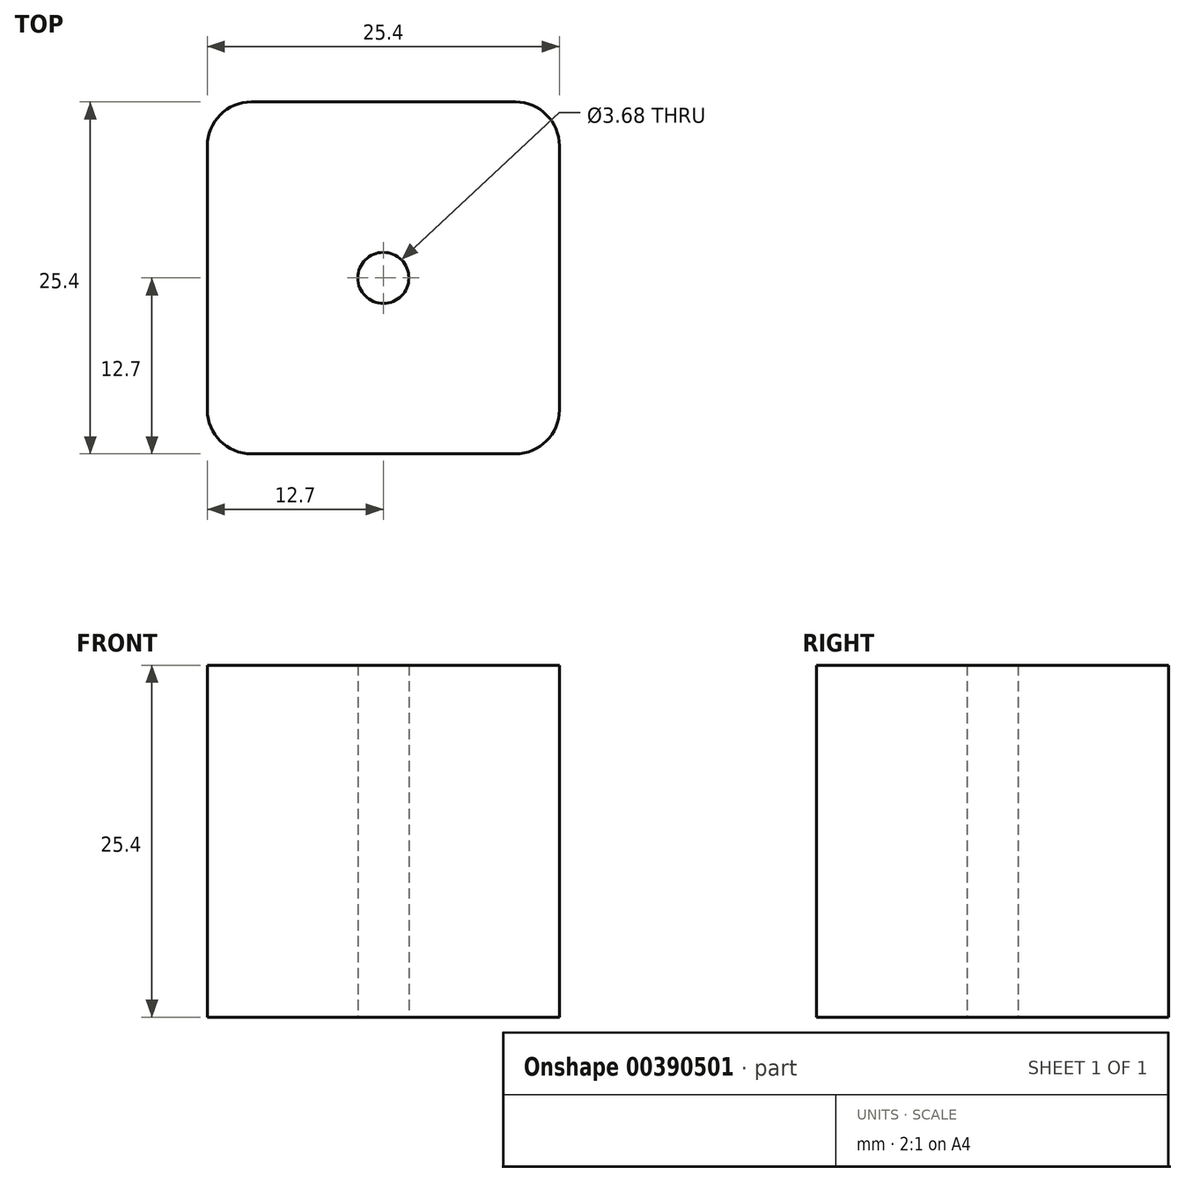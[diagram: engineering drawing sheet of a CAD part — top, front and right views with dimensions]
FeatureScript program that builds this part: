
annotation { "Feature Type Name" : "Feature", "Feature Type Description" : "" }
export const myFeature = defineFeature(function(context is Context, id is Id, definition is map)
    precondition{}
    {
        {
            var Q0;
            Q0=qCreatedBy(makeId("Top.planeOp"),FACE);
            var sketch = newSketch(context, id + "F0", { "sketchPlane" : qUnion([Q0])});
            skLineSegment(sketch, "E0.bottom", {"start": v(-9.53, 12.7) * mm, "end": v(9.53, 12.7) * mm});
            skLineSegment(sketch, "E0.top", {"start": v(-9.52, -12.7) * mm, "end": v(9.52, -12.7) * mm});
            skLineSegment(sketch, "E0.left", {"start": v(-12.7, 9.53) * mm, "end": v(-12.7, -9.52) * mm});
            skLineSegment(sketch, "E0.right", {"start": v(12.7, 9.53) * mm, "end": v(12.7, -9.53) * mm});
            skPoint(sketch, "E0.middle", {"position": v(0, 0) * mm});
            skPoint(sketch, "E1.visualSharp", {"position": v(-12.7, 12.7) * mm});
            skArc(sketch, "E1.filletArc", {"start": v(-9.53, 12.7) * mm, "mid": v(-11.77, 11.77) * mm, "end": v(-12.7, 9.53) * mm});
            skPoint(sketch, "E2.visualSharp", {"position": v(12.7, 12.7) * mm});
            skArc(sketch, "E2.filletArc", {"start": v(12.7, 9.53) * mm, "mid": v(11.77, 11.77) * mm, "end": v(9.53, 12.7) * mm});
            skPoint(sketch, "E3.visualSharp", {"position": v(-12.7, -12.7) * mm});
            skArc(sketch, "E3.filletArc", {"start": v(-12.7, -9.52) * mm, "mid": v(-11.77, -11.77) * mm, "end": v(-9.52, -12.7) * mm});
            skPoint(sketch, "E4.visualSharp", {"position": v(12.7, -12.7) * mm});
            skArc(sketch, "E4.filletArc", {"start": v(9.52, -12.7) * mm, "mid": v(11.77, -11.77) * mm, "end": v(12.7, -9.53) * mm});
            skCircle(sketch, "E5", {"center": v(0, 0) * mm, "radius": 1.84 * mm});
            skSolve(sketch);
        }
        {
            var Q0;
            Q0 = qSketchRegion(id + "F0", true);
            extrude(context, id + "F1", {"entities" : qUnion([Q0]), "endBound" : BoundingType.SYMMETRIC, "depth" : 25.4 * mm});
        }
    });
